FCSTD DOCUMENT  (FreeCAD 1.0R39319 (Git))
Label: legs
License: All rights reserved
LicenseURL: http://en.wikipedia.org/wiki/All_rights_reserved
objects: App::FeaturePython×23, App::Link×15, Assembly::JointGroup×1, Assembly::AssemblyObject×1
EXTERNAL_REF file=../parts/steel-profile-40x40x400.FCStd obj=Part
EXTERNAL_REF file=../parts/x-stepper-mounting-profile.FCStd obj=Part

FEATURE [App::Link] steel_profile_40x40x400  label="steel-profile-40x40x400"
  LinkPlacement = pos=(0,0,7.8701e-12) rot=(0,0,1;0rad)
  LinkedObject = -> <external ../parts/steel-profile-40x40x400.FCStd>#Part
  Placement = pos=(0,0,7.8701e-12) rot=(0,0,1;0rad)
FEATURE [App::FeaturePython] GroundedJoint  # Assembly grounded joint (typed FeaturePython)
  ObjectToGround = -> steel_profile_40x40x400
  Placement = pos=(0,0,7.8701e-12) rot=(0,0,1;0rad)
FEATURE [App::Link] steel_profile_40x40x401  label="steel-profile-40x40x401"
  LinkedObject = -> <external ../parts/steel-profile-40x40x400.FCStd>#Part
FEATURE [App::Link] steel_profile_40x40x402  label="steel-profile-40x40x402"
  LinkPlacement = pos=(40,40,-9.72909e-07) rot=(0,0.707107,0.707107;3.14159rad)
  LinkedObject = -> <external ../parts/steel-profile-40x40x400.FCStd>#Part
  Placement = pos=(40,40,-9.72909e-07) rot=(0,0.707107,0.707107;3.14159rad)
FEATURE [App::Link] steel_profile_40x40x403  label="steel-profile-40x40x403"
  LinkPlacement = pos=(-400,0,400) rot=(4.1e-05,1,0.000414;3.14076rad)
  LinkedObject = -> <external ../parts/steel-profile-40x40x400.FCStd>#Part
  Placement = pos=(-400,0,400) rot=(4.1e-05,1,0.000414;3.14076rad)
FEATURE [App::Link] steel_profile_40x40x404  label="steel-profile-40x40x404"
  LinkPlacement = pos=(-440,440,0) rot=(0.99998,0.004685,0.004188;1.57079rad)
  LinkedObject = -> <external ../parts/steel-profile-40x40x400.FCStd>#Part
  Placement = pos=(-440,440,0) rot=(0.99998,0.004685,0.004188;1.57079rad)
FEATURE [App::Link] steel_profile_40x40x405  label="steel-profile-40x40x405"
  LinkPlacement = pos=(0,440,0) rot=(0,0,1;0rad)
  LinkedObject = -> <external ../parts/steel-profile-40x40x400.FCStd>#Part
  Placement = pos=(0,440,0) rot=(0,0,1;0rad)
FEATURE [App::Link] steel_profile_40x40x406  label="steel-profile-40x40x406"
  LinkPlacement = pos=(0,440,0) rot=(-0.003469,0.999988,-0.003488;4.71178rad)
  LinkedObject = -> <external ../parts/steel-profile-40x40x400.FCStd>#Part
  Placement = pos=(0,440,0) rot=(-0.003469,0.999988,-0.003488;4.71178rad)
FEATURE [App::Link] steel_profile_40x40x407  label="steel-profile-40x40x407"
  LinkPlacement = pos=(-9.9e-15,1.7e-15,-3e-16) rot=(0.000745,0.999999,0.000745;4.71239rad)
  LinkedObject = -> <external ../parts/steel-profile-40x40x400.FCStd>#Part
  Placement = pos=(-9.9e-15,1.7e-15,-3e-16) rot=(0.000745,0.999999,0.000745;4.71239rad)
FEATURE [App::FeaturePython] GroundedJoint001  # Assembly grounded joint (typed FeaturePython)
  ObjectToGround = -> steel_profile_40x40x402
  Placement = pos=(40,40,-9.72909e-07) rot=(0,0.707107,0.707107;3.14159rad)
FEATURE [App::FeaturePython] GroundedJoint002  # Assembly grounded joint (typed FeaturePython)
  ObjectToGround = -> steel_profile_40x40x407
  Placement = pos=(-9.9e-15,1.7e-15,-3e-16) rot=(0.000745,0.999999,0.000745;4.71239rad)
FEATURE [App::FeaturePython] GroundedJoint003  # Assembly grounded joint (typed FeaturePython)
  ObjectToGround = -> steel_profile_40x40x405
  Placement = pos=(8.20807e-06,440,-1.75932e-05) rot=(0,0,1;0rad)
FEATURE [App::FeaturePython] GroundedJoint004  # Assembly grounded joint (typed FeaturePython)
  ObjectToGround = -> steel_profile_40x40x406
  Placement = pos=(3.27425e-05,440,1.2557e-05) rot=(-0.003469,0.999988,-0.003488;4.71178rad)
FEATURE [App::FeaturePython] Joint  label="Distance"  # Assembly joint (typed FeaturePython)
  Activated = true
  AngleMax = 0
  AngleMin = 0
  Detach1 = false
  Detach2 = false
  Distance = 0
  Distance2 = 0
  EnableAngleMax = false
  EnableAngleMin = false
  EnableLengthMax = false
  EnableLengthMin = false
  JointType = 5 (Distance)
  LengthMax = 0
  LengthMin = 0
  Placement1 = pos=(40,20,200) rot=(-0.57735,-0.57735,0.57735;2.0944rad)
  Placement2 = pos=(20,20,400) rot=(0,0,1;0rad)
  Reference1 = -> Assembly [steel_profile_40x40x404.Body.Face3,steel_profile_40x40x404.Body.Vertex5]
  Reference2 = -> Assembly [steel_profile_40x40x406.Body.Face14,steel_profile_40x40x406.Body.Vertex18]
FEATURE [App::FeaturePython] Joint001  label="Distance001"  # Assembly joint (typed FeaturePython)
  Activated = true
  AngleMax = 0
  AngleMin = 0
  Detach1 = false
  Detach2 = false
  Distance = 0
  Distance2 = 0
  EnableAngleMax = false
  EnableAngleMin = false
  EnableLengthMax = false
  EnableLengthMin = false
  JointType = 5 (Distance)
  LengthMax = 0
  LengthMin = 0
  Placement1 = pos=(20,20,400) rot=(0,0,1;0rad)
  Placement2 = pos=(20,40,200) rot=(0,-0.707107,0.707107;3.14159rad)
  Reference1 = -> Assembly [steel_profile_40x40x404.Body.Face14,steel_profile_40x40x404.Body.Vertex22]
  Reference2 = -> Assembly [steel_profile_40x40x403.Body.Face5,steel_profile_40x40x403.Body.Vertex9]
FEATURE [App::FeaturePython] Joint002  label="Parallel"  # Assembly joint (typed FeaturePython)
  Activated = true
  AngleMax = 0
  AngleMin = 0
  Detach1 = false
  Detach2 = false
  Distance = 0
  Distance2 = 0
  EnableAngleMax = false
  EnableAngleMin = false
  EnableLengthMax = false
  EnableLengthMin = false
  JointType = 6 (Parallel)
  LengthMax = 0
  LengthMin = 0
  Placement1 = pos=(2,40,0) rot=(0,-0.707107,0.707107;3.14159rad)
  Placement2 = pos=(40,2,400) rot=(-0.57735,-0.57735,0.57735;2.0944rad)
  Reference1 = -> Assembly [steel_profile_40x40x404.Body.Face5,steel_profile_40x40x404.Body.Vertex11]
  Reference2 = -> Assembly [steel_profile_40x40x406.Body.Face3,steel_profile_40x40x406.Body.Vertex6]
FEATURE [App::FeaturePython] Joint003  label="Distance002"  # Assembly joint (typed FeaturePython)
  Activated = true
  AngleMax = 0
  AngleMin = 0
  Detach1 = false
  Detach2 = false
  Distance = 0
  Distance2 = 0
  EnableAngleMax = false
  EnableAngleMin = false
  EnableLengthMax = false
  EnableLengthMin = false
  JointType = 5 (Distance)
  LengthMax = 0
  LengthMin = 0
  Placement1 = pos=(20,-9e-16,200) rot=(-1,0,0;1.5708rad)
  Placement2 = pos=(20,20,400) rot=(0,0,1;0rad)
  Reference1 = -> Assembly [steel_profile_40x40x404.Body.Face1,steel_profile_40x40x404.Body.Vertex4]
  Reference2 = -> Assembly [steel_profile_40x40x403.Body.Face14,steel_profile_40x40x403.Body.Vertex22]
FEATURE [App::FeaturePython] Joint004  label="Distance003"  # Assembly joint (typed FeaturePython)
  Activated = true
  AngleMax = 0
  AngleMin = 0
  Detach1 = false
  Detach2 = false
  Distance = 0
  Distance2 = 0
  EnableAngleMax = false
  EnableAngleMin = false
  EnableLengthMax = false
  EnableLengthMin = false
  JointType = 5 (Distance)
  LengthMax = 0
  LengthMin = 0
  Placement1 = pos=(20,40,200) rot=(0,-0.707107,0.707107;3.14159rad)
  Placement2 = pos=(40,20,200) rot=(-0.57735,-0.57735,0.57735;2.0944rad)
  Reference1 = -> Assembly [steel_profile_40x40x404.Body.Face5,steel_profile_40x40x404.Body.Face5]
  Reference2 = -> Assembly [steel_profile_40x40x406.Body.Face3,steel_profile_40x40x406.Body.Vertex6]
FEATURE [App::FeaturePython] Joint005  label="Distance004"  # Assembly joint (typed FeaturePython)
  Activated = true
  AngleMax = 0
  AngleMin = 0
  Detach1 = false
  Detach2 = false
  Distance = 0
  Distance2 = 0
  EnableAngleMax = false
  EnableAngleMin = false
  EnableLengthMax = false
  EnableLengthMin = false
  JointType = 5 (Distance)
  LengthMax = 0
  LengthMin = 0
  Placement1 = pos=(20,-9e-16,200) rot=(-1,0,0;1.5708rad)
  Placement2 = pos=(20,-9e-16,200) rot=(-1,0,0;1.5708rad)
  Reference1 = -> Assembly [steel_profile_40x40x403.Body.Face1,steel_profile_40x40x403.Body.Vertex4]
  Reference2 = -> Assembly [steel_profile_40x40x407.Body.Face1,steel_profile_40x40x407.Body.Vertex2]
FEATURE [App::FeaturePython] GroundedJoint005  # Assembly grounded joint (typed FeaturePython)
  ObjectToGround = -> steel_profile_40x40x404
  Placement = pos=(-440,440,-5.91282e-05) rot=(0.99998,0.004685,0.004188;1.57079rad)
FEATURE [App::FeaturePython] GroundedJoint006  # Assembly grounded joint (typed FeaturePython)
  ObjectToGround = -> steel_profile_40x40x403
  Placement = pos=(-400,-1.1921e-05,400) rot=(4.1e-05,1,0.000414;3.14076rad)
FEATURE [App::Link] steel_profile_40x40x408  label="steel-profile-40x40x408"
  LinkPlacement = pos=(-440,440,0) rot=(-0.01966,0.055819,0.998247;0.008893rad)
  LinkedObject = -> <external ../parts/steel-profile-40x40x400.FCStd>#Part
  Placement = pos=(-440,440,0) rot=(-0.01966,0.055819,0.998247;0.008893rad)
FEATURE [App::FeaturePython] Joint006  label="Fixed"  # Assembly joint (typed FeaturePython)
  Activated = true
  AngleMax = 0
  AngleMin = 0
  Detach1 = false
  Detach2 = false
  Distance = 0
  Distance2 = 0
  EnableAngleMax = false
  EnableAngleMin = false
  EnableLengthMax = false
  EnableLengthMin = false
  JointType = 0 (Fixed)
  LengthMax = 0
  LengthMin = 0
  Offset2 = pos=(0,0,0) rot=(0,0,-1;1.5708rad)
  Placement1 = pos=(20,-1e-15,0) rot=(0.707107,0,0.707107;3.14159rad)
  Placement2 = pos=(20,-1e-15,0) rot=(0.57735,0.57735,0.57735;2.0944rad)
  Reference1 = -> Assembly [steel_profile_40x40x408.Body.Edge3,steel_profile_40x40x408.Body.Edge3]
  Reference2 = -> Assembly [steel_profile_40x40x404.Body.Edge3,steel_profile_40x40x404.Body.Edge3]
FEATURE [App::FeaturePython] GroundedJoint007  # Assembly grounded joint (typed FeaturePython)
  ObjectToGround = -> steel_profile_40x40x408
  Placement = pos=(-440,440,-5.91282e-05) rot=(-0.01966,0.055819,0.998247;0.008893rad)
FEATURE [App::Link] steel_profile_40x40x411  label="steel-profile-40x40x411"
  LinkPlacement = pos=(0,440,360) rot=(0.000611,1,0.000434;4.71234rad)
  LinkedObject = -> <external ../parts/steel-profile-40x40x400.FCStd>#Part
  Placement = pos=(0,440,360) rot=(0.000611,1,0.000434;4.71234rad)
FEATURE [App::Link] steel_profile_40x40x412  label="steel-profile-40x40x412"
  LinkPlacement = pos=(0,440,400) rot=(0.714086,0.000272,-0.713488;3.14225rad)
  LinkedObject = -> <external ../parts/steel-profile-40x40x400.FCStd>#Part
  Placement = pos=(0,440,400) rot=(0.714086,0.000272,-0.713488;3.14225rad)
FEATURE [App::Link] steel_profile_40x40x413  label="steel-profile-40x40x413"
  LinkPlacement = pos=(0,0,360) rot=(-0.000373,1,0.000455;4.71239rad)
  LinkedObject = -> <external ../parts/steel-profile-40x40x400.FCStd>#Part
  Placement = pos=(0,0,360) rot=(-0.000373,1,0.000455;4.71239rad)
FEATURE [App::Link] steel_profile_40x40x414  label="steel-profile-40x40x414"
  LinkPlacement = pos=(0,80,400.402) rot=(0.707403,0.000269,-0.706811;3.14225rad)
  LinkedObject = -> <external ../parts/steel-profile-40x40x400.FCStd>#Part
  Placement = pos=(0,80,400.402) rot=(0.707403,0.000269,-0.706811;3.14225rad)
FEATURE [App::FeaturePython] Joint011  label="Fixed001"  # Assembly joint (typed FeaturePython)
  Activated = true
  AngleMax = 0
  AngleMin = 0
  Detach1 = false
  Detach2 = false
  Distance = 0
  Distance2 = 0
  EnableAngleMax = false
  EnableAngleMin = false
  EnableLengthMax = false
  EnableLengthMin = false
  JointType = 0 (Fixed)
  LengthMax = 0
  LengthMin = 0
  Offset2 = pos=(0,0,0) rot=(0,0,-1;1.5708rad)
  Placement1 = pos=(40,20,400) rot=(0.57735,0.57735,0.57735;4.18879rad)
  Placement2 = pos=(40,20,400) rot=(0,0.707107,0.707107;3.14159rad)
  Reference1 = -> Assembly [steel_profile_40x40x411.Body.Edge10,steel_profile_40x40x411.Body.Edge10]
  Reference2 = -> Assembly [steel_profile_40x40x408.Body.Edge10,steel_profile_40x40x408.Body.Edge10]
FEATURE [App::FeaturePython] Joint012  label="Fixed002"  # Assembly joint (typed FeaturePython)
  Activated = true
  AngleMax = 0
  AngleMin = 0
  Detach1 = false
  Detach2 = false
  Distance = 0
  Distance2 = 0
  EnableAngleMax = false
  EnableAngleMin = false
  EnableLengthMax = false
  EnableLengthMin = false
  JointType = 0 (Fixed)
  LengthMax = 0
  LengthMin = 0
  Offset2 = pos=(0,0,0) rot=(0,0,1;1.5708rad)
  Placement1 = pos=(40,20,400) rot=(0.57735,0.57735,0.57735;4.18879rad)
  Placement2 = pos=(-1e-15,20,0) rot=(-1,0,0;4.71239rad)
  Reference1 = -> Assembly [steel_profile_40x40x413.Body.Edge10,steel_profile_40x40x413.Body.Edge10]
  Reference2 = -> Assembly [steel_profile_40x40x403.Body.Edge21,steel_profile_40x40x403.Body.Edge21]
FEATURE [App::FeaturePython] GroundedJoint009  # Assembly grounded joint (typed FeaturePython)
  ObjectToGround = -> steel_profile_40x40x411
  Placement = pos=(6.13518e-06,440,360) rot=(0.000611,1,0.000434;4.71234rad)
FEATURE [App::FeaturePython] GroundedJoint011  # Assembly grounded joint (typed FeaturePython)
  ObjectToGround = -> steel_profile_40x40x413
  Placement = pos=(-3.96018e-05,6.13333e-05,360) rot=(-0.000373,1,0.000455;4.71239rad)
FEATURE [App::FeaturePython] GroundedJoint012  # Assembly grounded joint (typed FeaturePython)
  ObjectToGround = -> steel_profile_40x40x414
  Placement = pos=(0.00314416,79.9633,400.402) rot=(0.707403,0.000269,-0.706811;3.14225rad)
FEATURE [App::FeaturePython] Joint014  label="Distance010"  # Assembly joint (typed FeaturePython)
  Activated = true
  AngleMax = 0
  AngleMin = 0
  Detach1 = false
  Detach2 = false
  Distance = 0
  Distance2 = 0
  EnableAngleMax = false
  EnableAngleMin = false
  EnableLengthMax = false
  EnableLengthMin = false
  JointType = 5 (Distance)
  LengthMax = 0
  LengthMin = 0
FEATURE [App::Link] steel_profile_40x40x415  label="steel-profile-40x40x415"
  LinkPlacement = pos=(-440,40,418.3) rot=(-0.999999,0,0;1.5708rad)
  LinkedObject = -> <external ../parts/steel-profile-40x40x400.FCStd>#Part
  Placement = pos=(-440,40,418.3) rot=(-0.999999,0,0;1.5708rad)
FEATURE [App::Link] x_stepper_mounting_profile  label="x-stepper-mounting-profile"
  LinkPlacement = pos=(1.563e-13,440,354.54) rot=(0,0,-1;1.5708rad)
  LinkedObject = -> <external ../parts/x-stepper-mounting-profile.FCStd>#Part
  Placement = pos=(1.563e-13,440,354.54) rot=(0,0,-1;1.5708rad)
FEATURE [App::FeaturePython] Joint015  label="Fixed003"  # Assembly joint (typed FeaturePython)
  Activated = true
  AngleMax = 0
  AngleMin = 0
  Detach1 = false
  Detach2 = false
  Distance = 0
  Distance2 = 0
  EnableAngleMax = false
  EnableAngleMin = false
  EnableLengthMax = false
  EnableLengthMin = false
  JointType = 0 (Fixed)
  LengthMax = 0
  LengthMin = 0
  Placement1 = pos=(400,20,40) rot=(-0.57735,-0.57735,0.57735;4.18879rad)
  Placement2 = pos=(20,40,400) rot=(-0.707107,0,0.707107;3.14159rad)
  Reference1 = -> Assembly [x_stepper_mounting_profile.Body.Edge22,x_stepper_mounting_profile.Body.Edge22]
  Reference2 = -> Assembly [steel_profile_40x40x400.Body.Edge16,steel_profile_40x40x400.Body.Edge16]
FEATURE [App::FeaturePython] GroundedJoint013  # Assembly grounded joint (typed FeaturePython)
  ObjectToGround = -> steel_profile_40x40x412
  Placement = pos=(0.755161,439.295,400.39) rot=(0.714086,0.000272,-0.713488;3.14225rad)
FEATURE [Assembly::JointGroup] Joints
  Group = -> [GroundedJoint,GroundedJoint001,GroundedJoint002,GroundedJoint003,GroundedJoint004,Joint,Joint001,Joint002,Joint003,Joint004,Joint005,GroundedJoint005,GroundedJoint006,Joint006,GroundedJoint007,Joint011,Joint012,GroundedJoint009,GroundedJoint011,GroundedJoint012,Joint014,GroundedJoint013,Joint015]
FEATURE [Assembly::AssemblyObject] Assembly  label="legs"
  Group = -> [Joints,steel_profile_40x40x400,GroundedJoint,steel_profile_40x40x401,steel_profile_40x40x402,steel_profile_40x40x403,steel_profile_40x40x404,steel_profile_40x40x405,steel_profile_40x40x406,steel_profile_40x40x407,GroundedJoint001,GroundedJoint002,GroundedJoint003,GroundedJoint004,Joint,Joint001,Joint002,Joint003,Joint004,Joint005,GroundedJoint005,GroundedJoint006,steel_profile_40x40x408,Joint006,+15 more]
  Origin = -> Origin
  Type = Assembly

RESOLVED EXTERNAL PARTS (link-assembly join: the EXTERNAL_REF files above that resolve inside this repo's crawl, each included once):
---- part ../parts/steel-profile-40x40x400.FCStd = doc fcstd_9b98702d31b4 ----
FCSTD DOCUMENT  (FreeCAD 1.0R39319 (Git))
Label: steel-profile-40x40x400
License: All rights reserved
LicenseURL: http://en.wikipedia.org/wiki/All_rights_reserved
objects: Sketcher::SketchObject×1, PartDesign::Pad×1, PartDesign::Body×1, App::Part×1
note: 6 computed .brp shape members not serialized (recipe doc carries the construction recipe); baked Part::Feature solids carry a one-line shape summary decoded from their .brp

FEATURE [Sketcher::SketchObject] Sketch
  ArcFitTolerance = 1e-06
  AttachmentSupport = -> [XY_Plane001]
  FullyConstrained = true
  MakeInternals = false
  MapMode = 5
  sketch-geometry (18):
    g0: LineSegment StartX=2 StartY=-9e-16 StartZ=0 EndX=38 EndY=-9e-16 EndZ=0
    g1: LineSegment StartX=40 StartY=2 StartZ=0 EndX=40 EndY=38 EndZ=0
    g2: LineSegment StartX=38 StartY=40 StartZ=0 EndX=2 EndY=40 EndZ=0
    g3: LineSegment StartX=-1.3e-15 StartY=38 StartZ=0 EndX=-1.3e-15 EndY=2 EndZ=0
    g4: ArcOfCircle CenterX=2 CenterY=2 CenterZ=0 NormalX=0 NormalY=0 NormalZ=1 AngleXU=0 Radius=2 StartAngle=3.14159 EndAngle=4.71239
    g5: ArcOfCircle CenterX=38 CenterY=2 CenterZ=0 NormalX=0 NormalY=0 NormalZ=1 AngleXU=0 Radius=2 StartAngle=4.71239 EndAngle=6.28319
    g6: ArcOfCircle CenterX=38 CenterY=38 CenterZ=0 NormalX=0 NormalY=0 NormalZ=1 AngleXU=0 Radius=2 StartAngle=0 EndAngle=1.5708
    g7: ArcOfCircle CenterX=2 CenterY=38 CenterZ=0 NormalX=0 NormalY=0 NormalZ=1 AngleXU=0 Radius=2 StartAngle=1.5708 EndAngle=3.14159
    g8: LineSegment StartX=3 StartY=3 StartZ=0 EndX=37 EndY=3 EndZ=0
    g9: LineSegment StartX=37 StartY=3 StartZ=0 EndX=37 EndY=37 EndZ=0
    g10: LineSegment StartX=37 StartY=37 StartZ=0 EndX=3 EndY=37 EndZ=0
    g11: LineSegment StartX=3 StartY=37 StartZ=0 EndX=3 EndY=3 EndZ=0
    g12: LineSegment [constr] StartX=2 StartY=2 StartZ=0 EndX=3 EndY=3 EndZ=0
    g13: LineSegment [constr] StartX=38 StartY=2 StartZ=0 EndX=37 EndY=3 EndZ=0
    g14: LineSegment [constr] StartX=38 StartY=38 StartZ=0 EndX=37 EndY=37 EndZ=0
    g15: LineSegment [constr] StartX=2 StartY=38 StartZ=0 EndX=3 EndY=37 EndZ=0
    g16: GeomPoint [constr] X=-1.6e-15 Y=-1.1e-15 Z=0
    g17: GeomPoint [constr] X=40 Y=40 Z=0
  constraints (43):
    c: Tangent(g0,g4) = -1.5708
    c: Tangent(g0,g5) = -1.5708
    c: Tangent(g1,g5) = -1.5708
    c: Tangent(g1,g6) = -1.5708
    c: Tangent(g2,g6) = -1.5708
    c: Tangent(g2,g7) = -1.5708
    c: Tangent(g3,g7) = -1.5708
    c: Tangent(g3,g4) = -1.5708
    c: Horizontal(g0)
    c: Horizontal(g2)
    c: Vertical(g1)
    c: Vertical(g3)
    c: Equal(g4,g5)
    c: Equal(g5,g6)
    c: Equal(g6,g7)
    c: Coincident(g8,g9)
    c: Coincident(g9,g10)
    c: Coincident(g10,g11)
    c: Coincident(g11,g8)
    c: Horizontal(g8)
    c: Horizontal(g10)
    c: Vertical(g9)
    c: Vertical(g11)
    c: Coincident(g12,g4)
    c: Coincident(g12,g8)
    c: Coincident(g13,g5)
    c: Coincident(g13,g9)
    c: Coincident(g14,g6)
    c: Coincident(g14,g10)
    c: Coincident(g15,g7)
    c: Coincident(g15,g11)
    c: Perpendicular(g12,g13)
    c: Perpendicular(g13,g14)
    c: Perpendicular(g14,g15)
    c: PointOnObject(g16,g0)
    c: PointOnObject(g16,g3)
    c: PointOnObject(g17,g1)
    c: PointOnObject(g17,g2)
    c: Distance(g1,g3) = 40
    c: Distance(g0,g2) = 40
    c: Radius(g5) = 2
    c: Distance(g8,g0) = 3
    c: Coincident(g16,g-1)
FEATURE [PartDesign::Pad] Pad
  Direction = (0,0,1)
  Length = 400
  Length2 = 10
  Profile = -> Sketch
  ReferenceAxis = -> Sketch [N_Axis]
  Suppressed = false
  Type = 0
FEATURE [PartDesign::Body] Body
  AllowCompound = false
  Group = -> [Sketch,Pad]
  Origin = -> Origin001
  Tip = -> Pad
FEATURE [App::Part] Part  label="steel-profile-40x40x400"
  Group = -> [Body]
  Origin = -> Origin
---- part ../parts/x-stepper-mounting-profile.FCStd = doc fcstd_0d68abc6da6f ----
FCSTD DOCUMENT  (FreeCAD 1.0R39319 (Git))
Label: x-stepper-mounting-profile
License: All rights reserved
LicenseURL: http://en.wikipedia.org/wiki/All_rights_reserved
objects: Sketcher::SketchObject×2, PartDesign::Pad×1, PartDesign::Hole×1, PartDesign::Body×1, App::Part×1
note: 11 computed .brp shape members not serialized (recipe doc carries the construction recipe); baked Part::Feature solids carry a one-line shape summary decoded from their .brp

FEATURE [Sketcher::SketchObject] Sketch
  ArcFitTolerance = 1e-06
  AttachmentSupport = -> [YZ_Plane]
  FullyConstrained = true
  MakeInternals = false
  MapMode = 5
  Placement = pos=(0,0,0) rot=(0.57735,0.57735,0.57735;2.0944rad)
  sketch-geometry (18):
    g0: LineSegment StartX=2 StartY=0 StartZ=0 EndX=38 EndY=0 EndZ=0
    g1: LineSegment StartX=40 StartY=2 StartZ=0 EndX=40 EndY=38 EndZ=0
    g2: LineSegment StartX=38 StartY=40 StartZ=0 EndX=2 EndY=40 EndZ=0
    g3: LineSegment StartX=0 StartY=38 StartZ=0 EndX=0 EndY=2 EndZ=0
    g4: ArcOfCircle CenterX=2 CenterY=2 CenterZ=0 NormalX=0 NormalY=0 NormalZ=1 AngleXU=0 Radius=2 StartAngle=3.14159 EndAngle=4.71239
    g5: ArcOfCircle CenterX=38 CenterY=2 CenterZ=0 NormalX=0 NormalY=0 NormalZ=1 AngleXU=0 Radius=2 StartAngle=4.71239 EndAngle=6.28319
    g6: ArcOfCircle CenterX=38 CenterY=38 CenterZ=0 NormalX=0 NormalY=0 NormalZ=1 AngleXU=0 Radius=2 StartAngle=0 EndAngle=1.5708
    g7: ArcOfCircle CenterX=2 CenterY=38 CenterZ=0 NormalX=0 NormalY=0 NormalZ=1 AngleXU=0 Radius=2 StartAngle=1.5708 EndAngle=3.14159
    g8: LineSegment StartX=3 StartY=3 StartZ=0 EndX=37 EndY=3 EndZ=0
    g9: LineSegment StartX=37 StartY=3 StartZ=0 EndX=37 EndY=37 EndZ=0
    g10: LineSegment StartX=37 StartY=37 StartZ=0 EndX=3 EndY=37 EndZ=0
    g11: LineSegment StartX=3 StartY=37 StartZ=0 EndX=3 EndY=3 EndZ=0
    g12: LineSegment [constr] StartX=2 StartY=2 StartZ=0 EndX=3 EndY=3 EndZ=0
    g13: LineSegment [constr] StartX=38 StartY=2 StartZ=0 EndX=37 EndY=3 EndZ=0
    g14: LineSegment [constr] StartX=38 StartY=38 StartZ=0 EndX=37 EndY=37 EndZ=0
    g15: LineSegment [constr] StartX=2 StartY=38 StartZ=0 EndX=3 EndY=37 EndZ=0
    g16: GeomPoint [constr] X=0 Y=0 Z=0
    g17: GeomPoint [constr] X=40 Y=40 Z=0
  constraints (43):
    c: Tangent(g0,g4) = -1.5708
    c: Tangent(g0,g5) = -1.5708
    c: Tangent(g1,g5) = -1.5708
    c: Tangent(g1,g6) = -1.5708
    c: Tangent(g2,g6) = -1.5708
    c: Tangent(g2,g7) = -1.5708
    c: Tangent(g3,g7) = -1.5708
    c: Tangent(g3,g4) = -1.5708
    c: Horizontal(g0)
    c: Horizontal(g2)
    c: Vertical(g1)
    c: Vertical(g3)
    c: Equal(g4,g5)
    c: Equal(g5,g6)
    c: Equal(g6,g7)
    c: Coincident(g8,g9)
    c: Coincident(g9,g10)
    c: Coincident(g10,g11)
    c: Coincident(g11,g8)
    c: Horizontal(g8)
    c: Horizontal(g10)
    c: Vertical(g9)
    c: Vertical(g11)
    c: Coincident(g12,g4)
    c: Coincident(g12,g8)
    c: Coincident(g13,g5)
    c: Coincident(g13,g9)
    c: Coincident(g14,g6)
    c: Coincident(g14,g10)
    c: Coincident(g15,g7)
    c: Coincident(g15,g11)
    c: Perpendicular(g12,g13)
    c: Perpendicular(g13,g14)
    c: Perpendicular(g14,g15)
    c: PointOnObject(g16,g0)
    c: PointOnObject(g16,g3)
    c: PointOnObject(g17,g1)
    c: PointOnObject(g17,g2)
    c: Distance(g1,g3) = 40
    c: Distance(g0,g2) = 40
    c: Radius(g5) = 2
    c: Distance(g8,g0) = 3
    c: Coincident(g16,g-1)
FEATURE [PartDesign::Pad] Pad
  Direction = (1,0,0)
  Length = 400
  Length2 = 10
  Placement = pos=(0,0,0) rot=(1,1,1;2.0944rad)
  Profile = -> Sketch
  ReferenceAxis = -> Sketch [N_Axis]
  Suppressed = false
  Type = 0
FEATURE [Sketcher::SketchObject] Sketch001
  ArcFitTolerance = 1e-06
  AttachmentSupport = -> [Pad]
  FullyConstrained = false
  MakeInternals = false
  MapMode = 5
  Placement = pos=(0,8.8e-15,40) rot=(0,0,-1;1.5708rad)
  sketch-geometry (5):
    g0: LineSegment [constr] StartX=0 StartY=0 StartZ=0 EndX=0 EndY=400 EndZ=0
    g1: LineSegment [constr] StartX=0 StartY=0 StartZ=0 EndX=-40 EndY=0 EndZ=0
    g2: LineSegment [constr] StartX=0 StartY=200 StartZ=0 EndX=-40 EndY=200 EndZ=0
    g3: Circle CenterX=-20 CenterY=180 CenterZ=0 NormalX=0 NormalY=0 NormalZ=1 AngleXU=0 Radius=2
    g4: Circle CenterX=-20 CenterY=220 CenterZ=0 NormalX=0 NormalY=0 NormalZ=1 AngleXU=0 Radius=2
  constraints (12):
    c: Distance(g0) = 400
    c: Coincident(g0,g-1)
    c: Vertical(g0)
    c: Distance(g1) = 40
    c: Coincident(g1,g0)
    c: PointOnObject(g1,g-1)
    c: Distance(g2) = 40
    c: Symmetric(g0,g0,g2)
    c: Horizontal(g2)
    c: Diameter(g3) = 4
    c: Distance(g3,g2) = 20
    c: Diameter(g4) = 4
FEATURE [PartDesign::Hole] Hole
  BaseFeature = -> Pad
  CustomThreadClearance = 0
  Depth = 25
  DepthType = 0
  Diameter = 3.3
  DrillForDepth = false
  DrillPoint = 1
  DrillPointAngle = 118
  HoleCutCountersinkAngle = 90
  HoleCutCustomValues = false
  HoleCutDepth = 0
  HoleCutDiameter = 6.1
  HoleCutType = 0
  ModelThread = false
  Placement = pos=(0,0,0) rot=(1,1,1;2.0944rad)
  Profile = -> Sketch001
  Suppressed = false
  Tapered = false
  TaperedAngle = 90
  ThreadClass = 0
  ThreadDepth = 25
  ThreadDepthType = 0
  ThreadDirection = 0
  ThreadFit = 0
  ThreadSize = 11
  ThreadType = 1
  Threaded = true
  UseCustomThreadClearance = false
FEATURE [PartDesign::Body] Body
  AllowCompound = false
  Group = -> [Sketch,Pad,Sketch001,Hole]
  Origin = -> Origin
  Tip = -> Hole
FEATURE [App::Part] Part  label="x-stepper-mounting-profile"
  Group = -> [Body]
  Origin = -> Origin001
